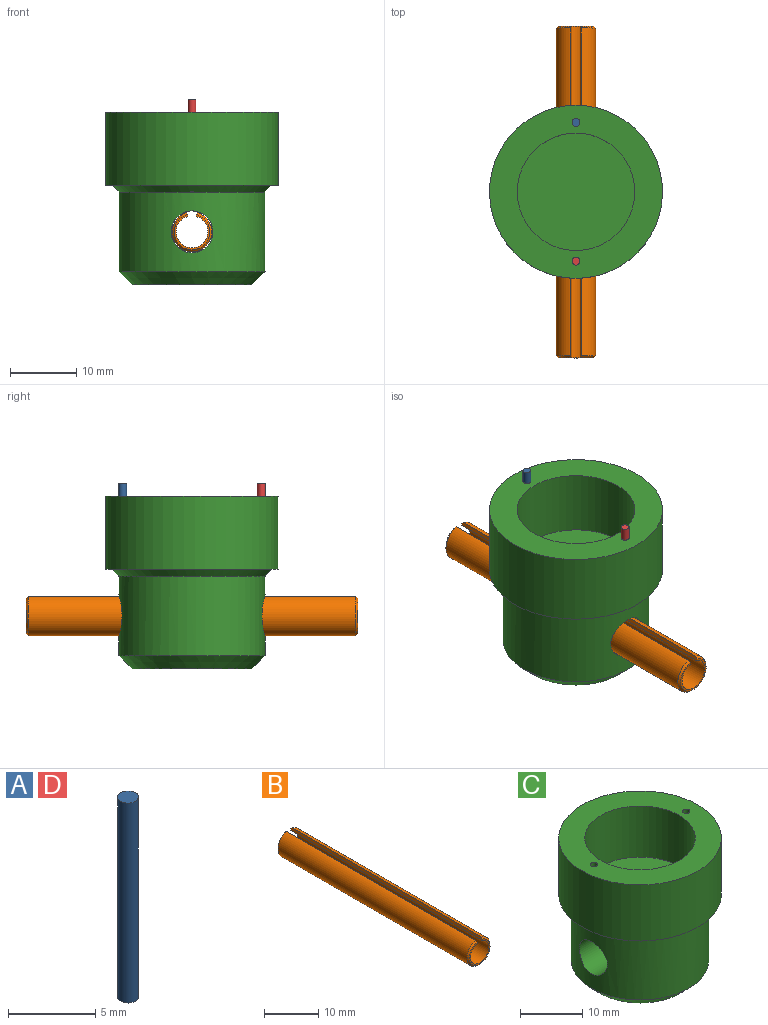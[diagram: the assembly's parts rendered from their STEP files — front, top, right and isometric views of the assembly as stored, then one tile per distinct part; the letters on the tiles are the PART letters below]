
ASSEMBLY  parts=4 mates=3
PART A: 3 faces, bbox 1.2x1.2x14 mm
  f0: cylinder r=0.6mm len=14mm, axis (0,0,-1), area 52.8mm2, adj f1,f2
  f1: plane 1.2x1.2mm, normal (0,0,1), area 1.1mm2, adj f0
  f2: plane 1.2x1.2mm, normal (0,0,-1), area 1.1mm2, adj f0
PART B: 8 faces, bbox 6x50x5.9 mm
  f0: cylinder r=3mm len=49.4mm, axis (0,1,0), area 853.6mm2, adj f4,f5,f6,f7
  f1: plane 5.4x5.31mm, normal (0,-1,0), area 4.4mm2, adj f3,f4,f6,f7
  f2: plane 5.4x5.31mm, normal (0,1,0), area 4.4mm2, adj f3,f5,f6,f7
  f3: cylinder r=2.4mm len=50mm, axis (0,1,0), area 691.2mm2, adj f1,f2,f6,f7
  f4: cone r=2.7mm half-angle=45deg, axis (0,1,0), area 7mm2, adj f0,f1,f6,f7
  f5: cone r=3mm half-angle=45deg, axis (0,-1,0), area 7mm2, adj f0,f2,f6,f7
  f6: plane 50x0.58mm, normal (-0.97,0,0.26), area 29.9mm2, adj f0,f1,f2,f3,f4,f5
  f7: plane 50x0.58mm, normal (0.97,0,0.26), area 29.9mm2, adj f0,f1,f2,f3,f4,f5
PART C: 14 faces, bbox 26.1x26.1x26 mm
  f0: cylinder r=11mm len=22mm, axis (0,0,-1), area 766.4mm2, adj f7,f8,f9,f11,f13
  f1: plane 18x18mm, normal (0,0,-1), area 254.5mm2, adj f7
  f2: cylinder r=13.03mm len=26.06mm, axis (0,0,-1), area 900.6mm2, adj f3,f4
  f3: plane 26.06x26.06mm, normal (0,0,1), area 285.1mm2, adj f2,f5,f10,f12
  f4: plane 26.06x26.06mm, normal (0,0,-1), area 81mm2, adj f2,f8
  f5: cylinder r=8.85mm len=17.7mm, axis (0,0,1), area 556.1mm2, adj f3,f6
  f6: plane 17.7x17.7mm, normal (0,0,1), area 246.1mm2, adj f5
  f7: cone r=11mm half-angle=45deg, axis (0,0,1), area 177.7mm2, adj f0,f1
  f8: cone r=12mm half-angle=45deg, axis (0,0,1), area 102.1mm2, adj f0,f4,f10,f12
  f9: cylinder r=3.15mm len=22mm, axis (1,0,0), area 426.4mm2, adj f0
  f10: cylinder r=0.6mm len=12mm, axis (0,0,1), area 45.2mm2, adj f3,f8,f11
  f11: plane 1.2x1.15mm, normal (0,0,1), area 1.1mm2, adj f0,f10
  f12: cylinder r=0.6mm len=12mm, axis (0,0,1), area 45.2mm2, adj f3,f8,f13
  f13: plane 1.2x1.15mm, normal (0,0,1), area 1.1mm2, adj f0,f12
PART D: same geometry as A
PLACE A rot(axis=(0,0,1),90deg) t=(16.3,26.79,12.45)mm
PLACE B t=(16.3,41.34,6.45)mm
PLACE C rot(axis=(0,0,1),90deg) t=(16.3,16.34,-1.55)mm
PLACE D rot(axis=(0,0,1),90deg) t=(16.3,5.89,12.45)mm
MATE fastened A.f0 <-> C.f10  axis (0,0,-1) through (16.3,26.79,12.45)mm
MATE fastened C.f9 <-> B.f0  axis (0,1,0) through (16.3,16.34,6.45)mm
MATE fastened D.f0 <-> C.f12  axis (0,0,-1) through (16.3,5.89,12.45)mm
